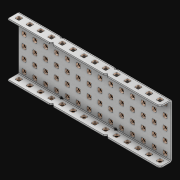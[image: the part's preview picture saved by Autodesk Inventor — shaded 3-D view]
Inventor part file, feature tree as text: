
AUTODESK INVENTOR PART (.ipt)
format: ipt  version: 2021 (Build 250183000, 183)  size: 3,169,792 bytes
history: native  units: in
note: dims shown in document units (in); Inventor stores cm internally (conversion verified against a paired STEP export)
features: extrude x99, other x98, sketch x4, thicken_offset x3, pattern_linear x3, imported_body x1
ambient origin geometry x8: Origin, YZ Plane, XZ Plane, XY Plane, X Axis, Y Axis, Z Axis, Center Point
bodies: Solid1 (feature_tree)
feature tree (208):
  thicken_offset  "Thicken1"
  thicken_offset  "Thicken2"
  thicken_offset  "Thicken3"
  pattern_linear  "Rectangular Pattern1"  Spacing1=0.001in  [1 undecoded]
  pattern_linear  "Rectangular Pattern2"  Spacing1=0.001in  [1 undecoded]
  pattern_linear  "Rectangular Pattern3"  Spacing1=0.182in  [1 undecoded]
  extrude  "Extrusion1"  Depth=0.063in TaperAngle=0.0deg
  sketch  "Sketch1"  dims[d0=0.001in]
  other  "Srf1"
  sketch  "Sketch2"  dims[d1=0.001in]
  other  "Srf2"
  sketch  "Sketch3"  dims[d2=0.001in]
  other  "Srf3"
  other  "Srf4"
  other  "Srf5"
  other  "Srf6"
  other  "Srf7"
  other  "Srf8"
  other  "Srf9"
  other  "Srf10"
  other  "Srf11"
  other  "Srf12"
  other  "Srf13"
  other  "Srf14"
  other  "Srf15"
  other  "Srf16"
  other  "Srf38"
  other  "Srf39"
  other  "Srf40"
  other  "Srf41"
  other  "Srf42"
  other  "Srf43"
  other  "Srf44"
  other  "Srf45"
  other  "Srf46"
  other  "Srf47"
  other  "Srf48"
  other  "Srf49"
  other  "Srf50"
  other  "Srf72"
  other  "Srf73"
  other  "Srf74"
  other  "Srf75"
  other  "Srf76"
  other  "Srf77"
  other  "Srf78"
  other  "Srf79"
  other  "Srf80"
  other  "Srf81"
  other  "Srf82"
  other  "Srf83"
  other  "Srf84"
  other  "Srf106"
  other  "Srf107"
  other  "Srf108"
  other  "Srf109"
  other  "Srf110"
  other  "Srf111"
  other  "Srf112"
  other  "Srf113"
  other  "Srf114"
  other  "Srf115"
  other  "Srf116"
  other  "Srf117"
  other  "Srf118"
  other  "Srf119"
  other  "Srf141"
  other  "Srf142"
  other  "Srf143"
  other  "Srf144"
  other  "Srf145"
  other  "Srf146"
  other  "Srf147"
  other  "Srf148"
  other  "Srf149"
  other  "Srf150"
  other  "Srf151"
  other  "Srf152"
  other  "Srf153"
  other  "Srf154"
  other  "Srf176"
  other  "Srf177"
  other  "Srf178"
  other  "Srf179"
  other  "Srf180"
  other  "Srf181"
  other  "Srf182"
  other  "Srf183"
  other  "Srf184"
  other  "Srf185"
  other  "Srf186"
  other  "Srf187"
  other  "Srf188"
  other  "Srf189"
  other  "Srf211"
  other  "Srf212"
  other  "Srf213"
  other  "Srf214"
  other  "Srf215"
  other  "Srf216"
  other  "Srf217"
  other  "Srf218"
  other  "Srf219"
  other  "Srf220"
  other  "Srf221"
  other  "Srf222"
  other  "Srf223"
  other  "Srf224"
  sketch  "Sketch4"  dims[d3=0.001in d4=0.001in d5=0.001in d6=0.182in d7=0.063in d8=0.0in d9=0.182in d10=0.063in d11=0.0in d12=0.182in d13=0.063in d14=0.0in d17=0.5in d18=5.5118in d20=0.5in d21=5.5118in d23=0.5in d24=1.9685in d26=0.5in d27=10.5in d28=0.0in]
  imported_body  "Imported1"
  extrude  "ExtrusionSrf1"  Depth=0.063in
  extrude  "ExtrusionSrf2"  Depth=0.063in TaperAngle=0.0deg
  extrude  "ExtrusionSrf3"  Depth=0.063in
  extrude  "ExtrusionSrf4"  Depth=0.063in TaperAngle=0.0deg
  extrude  "ExtrusionSrf5"  Depth=0.063in
  extrude  "ExtrusionSrf6"  Depth=0.063in
  extrude  "ExtrusionSrf7"  Depth=0.063in
  extrude  "ExtrusionSrf8"  Depth=0.063in
  extrude  "ExtrusionSrf9"  Depth=0.063in
  extrude  "ExtrusionSrf10"  Depth=0.063in
  extrude  "ExtrusionSrf11"  Depth=0.063in
  extrude  "ExtrusionSrf12"  TaperAngle=0.0deg  [1 undecoded]
  extrude  "ExtrusionSrf13"  [1 undecoded]
  extrude  "ExtrusionSrf14"  [1 undecoded]
  extrude  "ExtrusionSrf15"  [1 undecoded]
  extrude  "ExtrusionSrf16"  [1 undecoded]
  extrude  "ExtrusionSrf38"  [1 undecoded]
  extrude  "ExtrusionSrf39"  [1 undecoded]
  extrude  "ExtrusionSrf40"  [1 undecoded]
  extrude  "ExtrusionSrf41"  [1 undecoded]
  extrude  "ExtrusionSrf42"  [1 undecoded]
  extrude  "ExtrusionSrf43"  [1 undecoded]
  extrude  "ExtrusionSrf44"  [1 undecoded]
  extrude  "ExtrusionSrf45"  [1 undecoded]
  extrude  "ExtrusionSrf46"  [1 undecoded]
  extrude  "ExtrusionSrf47"  [1 undecoded]
  extrude  "ExtrusionSrf48"  [1 undecoded]
  extrude  "ExtrusionSrf49"  [1 undecoded]
  extrude  "ExtrusionSrf50"  [1 undecoded]
  extrude  "ExtrusionSrf72"  [1 undecoded]
  extrude  "ExtrusionSrf73"  [1 undecoded]
  extrude  "ExtrusionSrf74"  [1 undecoded]
  extrude  "ExtrusionSrf75"  [1 undecoded]
  extrude  "ExtrusionSrf76"  [1 undecoded]
  extrude  "ExtrusionSrf77"  [1 undecoded]
  extrude  "ExtrusionSrf78"  [1 undecoded]
  extrude  "ExtrusionSrf79"  [1 undecoded]
  extrude  "ExtrusionSrf80"  [1 undecoded]
  extrude  "ExtrusionSrf81"  [1 undecoded]
  extrude  "ExtrusionSrf82"  [1 undecoded]
  extrude  "ExtrusionSrf83"  [1 undecoded]
  extrude  "ExtrusionSrf84"  [1 undecoded]
  extrude  "ExtrusionSrf106"  [1 undecoded]
  extrude  "ExtrusionSrf107"  [1 undecoded]
  extrude  "ExtrusionSrf108"  [1 undecoded]
  extrude  "ExtrusionSrf109"  [1 undecoded]
  extrude  "ExtrusionSrf110"  [1 undecoded]
  extrude  "ExtrusionSrf111"  [1 undecoded]
  extrude  "ExtrusionSrf112"  [1 undecoded]
  extrude  "ExtrusionSrf113"  [1 undecoded]
  extrude  "ExtrusionSrf114"  [1 undecoded]
  extrude  "ExtrusionSrf115"  [1 undecoded]
  extrude  "ExtrusionSrf116"  [1 undecoded]
  extrude  "ExtrusionSrf117"  [1 undecoded]
  extrude  "ExtrusionSrf118"  [1 undecoded]
  extrude  "ExtrusionSrf119"  [1 undecoded]
  extrude  "ExtrusionSrf141"  [1 undecoded]
  extrude  "ExtrusionSrf142"  [1 undecoded]
  extrude  "ExtrusionSrf143"  [1 undecoded]
  extrude  "ExtrusionSrf144"  [1 undecoded]
  extrude  "ExtrusionSrf145"  [1 undecoded]
  extrude  "ExtrusionSrf146"  [1 undecoded]
  extrude  "ExtrusionSrf147"  [1 undecoded]
  extrude  "ExtrusionSrf148"  [1 undecoded]
  extrude  "ExtrusionSrf149"  [1 undecoded]
  extrude  "ExtrusionSrf150"  [1 undecoded]
  extrude  "ExtrusionSrf151"  [1 undecoded]
  extrude  "ExtrusionSrf152"  [1 undecoded]
  extrude  "ExtrusionSrf153"  [1 undecoded]
  extrude  "ExtrusionSrf154"  [1 undecoded]
  extrude  "ExtrusionSrf176"  [1 undecoded]
  extrude  "ExtrusionSrf177"  [1 undecoded]
  extrude  "ExtrusionSrf178"  [1 undecoded]
  extrude  "ExtrusionSrf179"  [1 undecoded]
  extrude  "ExtrusionSrf180"  [1 undecoded]
  extrude  "ExtrusionSrf181"  [1 undecoded]
  extrude  "ExtrusionSrf182"  [1 undecoded]
  extrude  "ExtrusionSrf183"  [1 undecoded]
  extrude  "ExtrusionSrf184"  [1 undecoded]
  extrude  "ExtrusionSrf185"  [1 undecoded]
  extrude  "ExtrusionSrf186"  [1 undecoded]
  extrude  "ExtrusionSrf187"  [1 undecoded]
  extrude  "ExtrusionSrf188"  [1 undecoded]
  extrude  "ExtrusionSrf189"  [1 undecoded]
  extrude  "ExtrusionSrf211"  [1 undecoded]
  extrude  "ExtrusionSrf212"  [1 undecoded]
  extrude  "ExtrusionSrf213"  [1 undecoded]
  extrude  "ExtrusionSrf214"  [1 undecoded]
  extrude  "ExtrusionSrf215"  [1 undecoded]
  extrude  "ExtrusionSrf216"  [1 undecoded]
  extrude  "ExtrusionSrf217"  [1 undecoded]
  extrude  "ExtrusionSrf218"  [1 undecoded]
  extrude  "ExtrusionSrf219"  [1 undecoded]
  extrude  "ExtrusionSrf220"  [1 undecoded]
  extrude  "ExtrusionSrf221"  [1 undecoded]
  extrude  "ExtrusionSrf222"  [1 undecoded]
  extrude  "ExtrusionSrf223"  [1 undecoded]
  extrude  "ExtrusionSrf224"  [1 undecoded]
note: 90 required parameter values undecoded (feature->parameter linkage not recoverable at this tier; creation-order binding heuristic only, values carry confidence <= 0.55)
